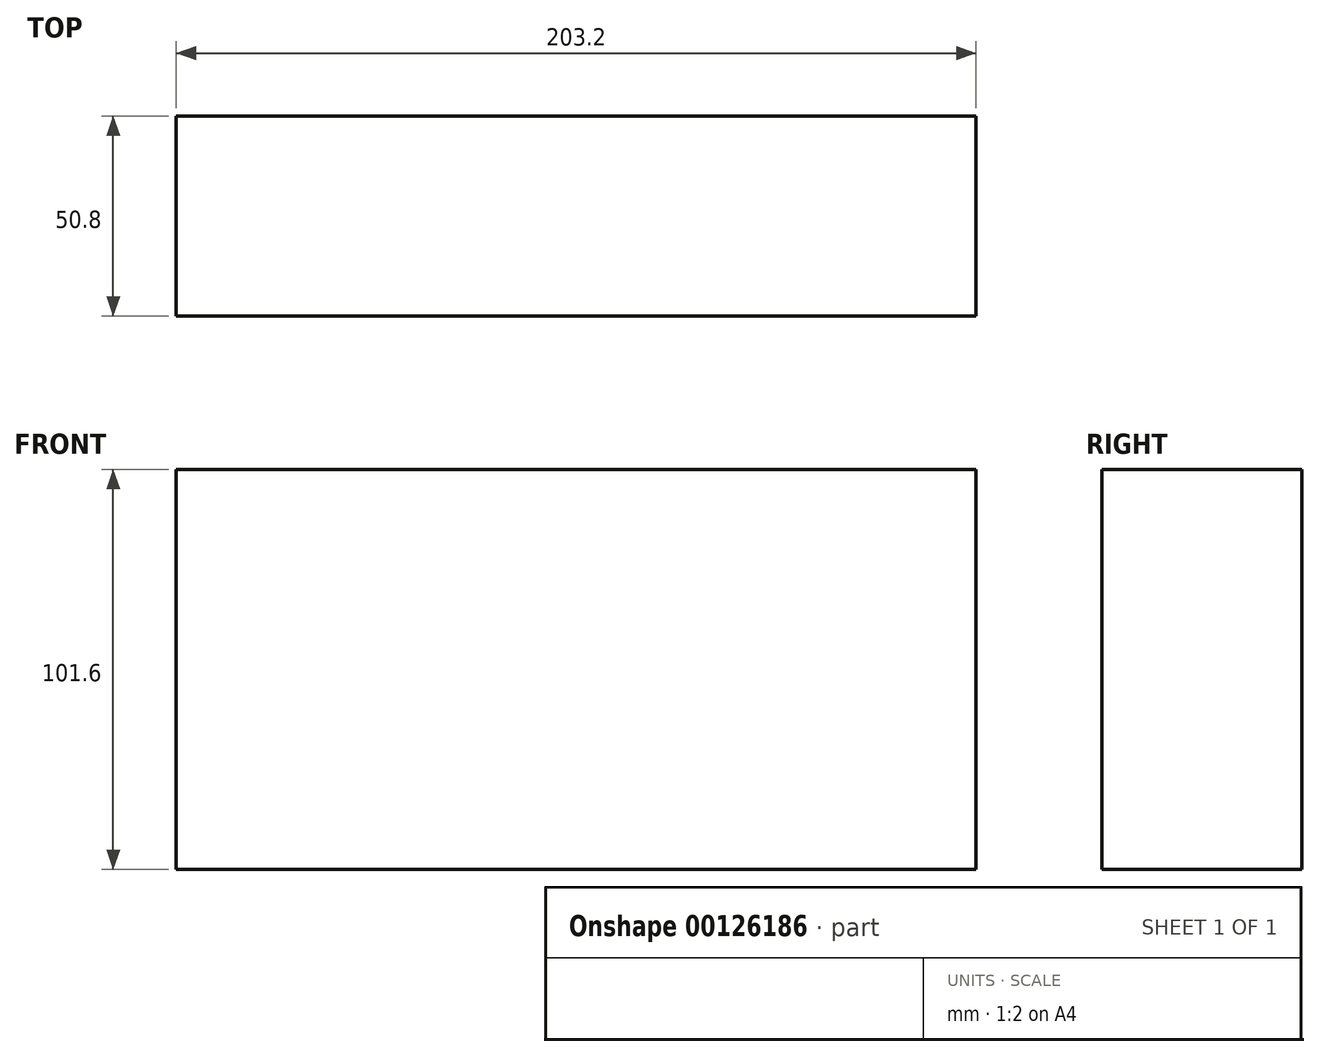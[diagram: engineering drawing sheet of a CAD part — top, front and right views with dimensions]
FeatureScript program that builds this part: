
annotation { "Feature Type Name" : "Feature", "Feature Type Description" : "" }
export const myFeature = defineFeature(function(context is Context, id is Id, definition is map)
    precondition{}
    {
        {
            var Q0;
            Q0=qCreatedBy(makeId("Front.planeOp"),FACE);
            var sketch = newSketch(context, id + "F0", { "sketchPlane" : qUnion([Q0])});
            skLineSegment(sketch, "E0.bottom", {"start": v(-100.06, 50.64) * mm, "end": v(103.14, 50.64) * mm});
            skLineSegment(sketch, "E0.top", {"start": v(-100.06, -50.96) * mm, "end": v(103.14, -50.96) * mm});
            skLineSegment(sketch, "E0.left", {"start": v(-100.06, 50.64) * mm, "end": v(-100.06, -50.96) * mm});
            skLineSegment(sketch, "E0.right", {"start": v(103.14, 50.64) * mm, "end": v(103.14, -50.96) * mm});
            skLineSegment(sketch, "E1", {"start": v(-100.06, 0) * mm, "end": v(103.14, 0) * mm, "construction": true});
            skLineSegment(sketch, "E2", {"start": v(0, 50.64) * mm, "end": v(0, -50.96) * mm, "construction": true});
            skSolve(sketch);
        }
        {
            var Q0;
            Q0 = qSketchRegion(id + "F0", true);
            extrude(context, id + "F1", {"entities" : qUnion([Q0]), "endBound" : BoundingType.SYMMETRIC, "depth" : 50.8 * mm});
        }
    });
